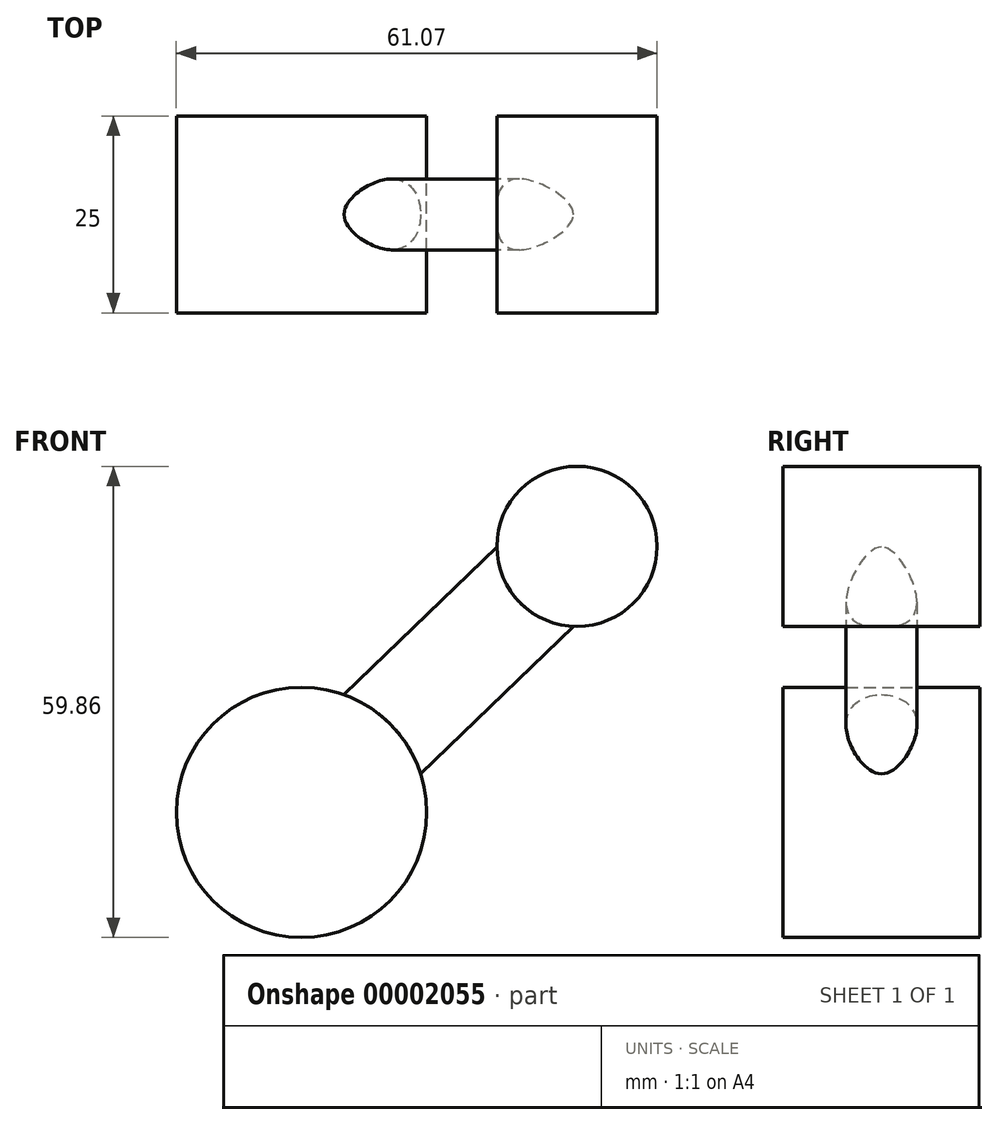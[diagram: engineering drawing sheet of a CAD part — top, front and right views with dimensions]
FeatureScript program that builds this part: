
annotation { "Feature Type Name" : "Feature", "Feature Type Description" : "" }
export const myFeature = defineFeature(function(context is Context, id is Id, definition is map)
    precondition{}
    {
        {
            var Q0;
            Q0=qCreatedBy(makeId("Front.planeOp"),FACE);
            var sketch = newSketch(context, id + "F0", { "sketchPlane" : qUnion([Q0])});
            skCircle(sketch, "E0", {"center": v(0, 0) * mm, "radius": 15.9 * mm});
            skCircle(sketch, "E1", {"center": v(0, 0) * mm, "radius": 7.7 * mm});
            skCircle(sketch, "E2", {"center": v(34.99, 33.79) * mm, "radius": 10.18 * mm});
            skCircle(sketch, "E3", {"center": v(34.99, 33.79) * mm, "radius": 4.87 * mm});
            skLineSegment(sketch, "E4", {"start": v(0, 0) * mm, "end": v(34.99, 33.79) * mm});
            skLineSegment(sketch, "E5", {"start": v(0, 0) * mm, "end": v(39.74, 0) * mm, "construction": true});
            skPoint(sketch, "E6", {"position": v(17.5, 16.9) * mm});
            skSolve(sketch);
        }
        {
            var Q0;
            Q0=sQuery(id+"F0.wireOp",EDGE,"E4");
            var Q1;
            Q1=sQuery(id+"F0.wireOp",VERTEX,"E6");
            cPlane(context, id + "F1", {"entities" : qUnion([Q0, Q1]), "cplaneType" : CPlaneType.CURVE_POINT, "offset" : 150 * mm, "width" : 150 * mm, "height" : 150 * mm});
        }
        {
            var Q0;
            Q0=qCreatedBy(id+"F1.planeOp",FACE);
            var sketch = newSketch(context, id + "F2", { "sketchPlane" : qUnion([Q0])});
            skCircle(sketch, "E7", {"center": v(0, 0) * mm, "radius": 7 * mm});
            skCircle(sketch, "E8", {"center": v(0, 0) * mm, "radius": 4.5 * mm});
            skFitSpline(sketch, "E9", {"points": [v(0, 7) * mm, v(4.5, 0) * mm, v(0, -7) * mm, v(-4.5, 0) * mm, v(0, 7) * mm]});
            skLineSegment(sketch, "E10", {"start": v(0, 7) * mm, "end": v(0, -7) * mm});
            skSolve(sketch);
        }
        {
            var Q0;
            {var subQ2=sQuery(id+"F0.wireOp",EDGE,"E0");Q0=makeQuery(id+"F0.imprint","IMPRINT",FACE,{"disambiguationData":[TD([[makeQuery(id+"F0.imprint","IMPRINT",EDGE,{"derivedFrom":subQ2}),1.0]])]});}
            var Q1;
            {var subQ1=sQuery(id+"F0.wireOp",EDGE,"E1");Q1=makeQuery(id+"F0.imprint","IMPRINT",FACE,{"disambiguationData":[TD([[makeQuery(id+"F0.imprint","IMPRINT",EDGE,{"derivedFrom":subQ1}),1.0]])]});}
            var Q2;
            {var subQ2=sQuery(id+"F0.wireOp",EDGE,"E2");Q2=makeQuery(id+"F0.imprint","IMPRINT",FACE,{"disambiguationData":[TD([[makeQuery(id+"F0.imprint","IMPRINT",EDGE,{"derivedFrom":subQ2}),1.0]])]});}
            var Q3;
            {var subQ1=sQuery(id+"F0.wireOp",EDGE,"E3");Q3=makeQuery(id+"F0.imprint","IMPRINT",FACE,{"disambiguationData":[TD([[makeQuery(id+"F0.imprint","IMPRINT",EDGE,{"derivedFrom":subQ1}),1.0]])]});}
            extrude(context, id + "F3", {"entities" : qUnion([Q0, Q1, Q2, Q3]), "endBound" : BoundingType.SYMMETRIC, "depth" : 25 * mm});
        }
        {
            var Q0;
            {var subQ0=sQuery(id+"F2.wireOp",EDGE,"E10");var subQ1=sQuery(id+"F2.wireOp",EDGE,"E8");var subQ2=makeQuery(id+"F2.imprint","INTERSECT",VERTEX,{"disambiguationData":[OD(0.0)],"derivedFrom":[subQ1,subQ0]});Q0=makeQuery(id+"F2.imprint","IMPRINT",FACE,{"disambiguationData":[TD([[makeQuery(id+"F2.imprint","IMPRINT",EDGE,{"disambiguationData":[TD([[subQ2,1.0]])],"derivedFrom":subQ1}),-1.0]])]});}
            var Q1;
            {var subQ0=sQuery(id+"F2.wireOp",EDGE,"E10");var subQ1=sQuery(id+"F2.wireOp",EDGE,"E8");var subQ3=makeQuery(id+"F2.imprint","INTERSECT",VERTEX,{"disambiguationData":[OD(0.0)],"derivedFrom":[subQ1,subQ0]});Q1=makeQuery(id+"F2.imprint","IMPRINT",FACE,{"disambiguationData":[TD([[makeQuery(id+"F2.imprint","IMPRINT",EDGE,{"disambiguationData":[TD([[subQ3,1.0]])],"derivedFrom":subQ1}),1.0]])]});}
            var Q2;
            {var subQ1=sQuery(id+"F2.wireOp",EDGE,"E8");var subQ3=sQuery(id+"F2.wireOp",EDGE,"E9");var subQ5=makeQuery(id+"F2.imprint","INTERSECT",VERTEX,{"disambiguationData":[OD(0.0)],"derivedFrom":[subQ1,subQ3]});Q2=makeQuery(id+"F2.imprint","IMPRINT",FACE,{"disambiguationData":[TD([[makeQuery(id+"F2.imprint","IMPRINT",EDGE,{"disambiguationData":[TD([[subQ5,1.0]])],"derivedFrom":subQ1}),-1.0]])]});}
            var Q3;
            {var subQ1=sQuery(id+"F2.wireOp",EDGE,"E8");var subQ3=sQuery(id+"F2.wireOp",EDGE,"E9");var subQ5=makeQuery(id+"F2.imprint","INTERSECT",VERTEX,{"disambiguationData":[OD(1.0)],"derivedFrom":[subQ1,subQ3]});Q3=makeQuery(id+"F2.imprint","IMPRINT",FACE,{"disambiguationData":[TD([[makeQuery(id+"F2.imprint","IMPRINT",EDGE,{"disambiguationData":[TD([[subQ5,-1.0]])],"derivedFrom":subQ1}),-1.0]])]});}
            var Q4;
            {var subQ0=sQuery(id+"F2.wireOp",EDGE,"E10");var subQ1=sQuery(id+"F2.wireOp",EDGE,"E8");var subQ3=makeQuery(id+"F2.imprint","INTERSECT",VERTEX,{"disambiguationData":[OD(0.0)],"derivedFrom":[subQ1,subQ0]});Q4=makeQuery(id+"F2.imprint","IMPRINT",FACE,{"disambiguationData":[TD([[makeQuery(id+"F2.imprint","IMPRINT",EDGE,{"disambiguationData":[TD([[subQ3,-1.0]])],"derivedFrom":subQ1}),1.0]])]});}
            var Q5;
            {var subQ0=sQuery(id+"F2.wireOp",EDGE,"E10");var subQ1=sQuery(id+"F2.wireOp",EDGE,"E8");var subQ2=makeQuery(id+"F2.imprint","INTERSECT",VERTEX,{"disambiguationData":[OD(0.0)],"derivedFrom":[subQ1,subQ0]});Q5=makeQuery(id+"F2.imprint","IMPRINT",FACE,{"disambiguationData":[TD([[makeQuery(id+"F2.imprint","IMPRINT",EDGE,{"disambiguationData":[TD([[subQ2,-1.0]])],"derivedFrom":subQ1}),-1.0]])]});}
            extrude(context, id + "F4", {"entities" : qUnion([Q0, Q1, Q2, Q3, Q4, Q5]), "operationType" : NewBodyOperationType.ADD, "endBound" : BoundingType.SYMMETRIC, "depth" : 60 * mm});
        }
    });
